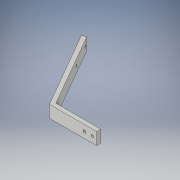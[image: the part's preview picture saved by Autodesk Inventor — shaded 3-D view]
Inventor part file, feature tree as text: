
AUTODESK INVENTOR PART (.ipt)
format: ipt  version: 2017 (Build 210142000, 142)  size: 123,392 bytes
history: native  units: in
note: dims shown in document units (in); Inventor stores cm internally (conversion verified against a paired STEP export)
features: sketch x3, hole x2, projected_geometry x2, extrude x1
ambient origin geometry x8: Origin, YZ Plane, XZ Plane, XY Plane, X Axis, Y Axis, Z Axis, Center Point
bodies: Solid1 (feature_tree)
feature tree (8):
  extrude  "Extrusion1"  Depth=0.25in
  hole  "Hole1"  [1 undecoded]
  hole  "Hole2"  [1 undecoded]
  sketch  "Sketch1"  dims[d0=60.0deg d2=0.25in]
  sketch  "Sketch2"  dims[d3=0.25in d4=0.0in]
  projected_geometry  "Projected Loop1"
  sketch  "Sketch3"  dims[d5=4.5in d6=2.75in d7=0.75in d8=0.0in d9=0.25in d10=0.75in d11=0.375in d12=0.375in d13=0.175in d14=0.75in d15=0.375in d16=0.25in d17=0.5635in d18=1.0in d19=0.8108in d20=0.25in d21=1.75in d22=0.375in d23=0.375in d24=0.16in d25=0.75in d26=0.375in d27=0.25in d28=0.5635in d29=1.0in d30=0.8108in]
  projected_geometry  "Projected Loop2"
note: 2 required parameter values undecoded (feature->parameter linkage not recoverable at this tier; creation-order binding heuristic only, values carry confidence <= 0.55)
